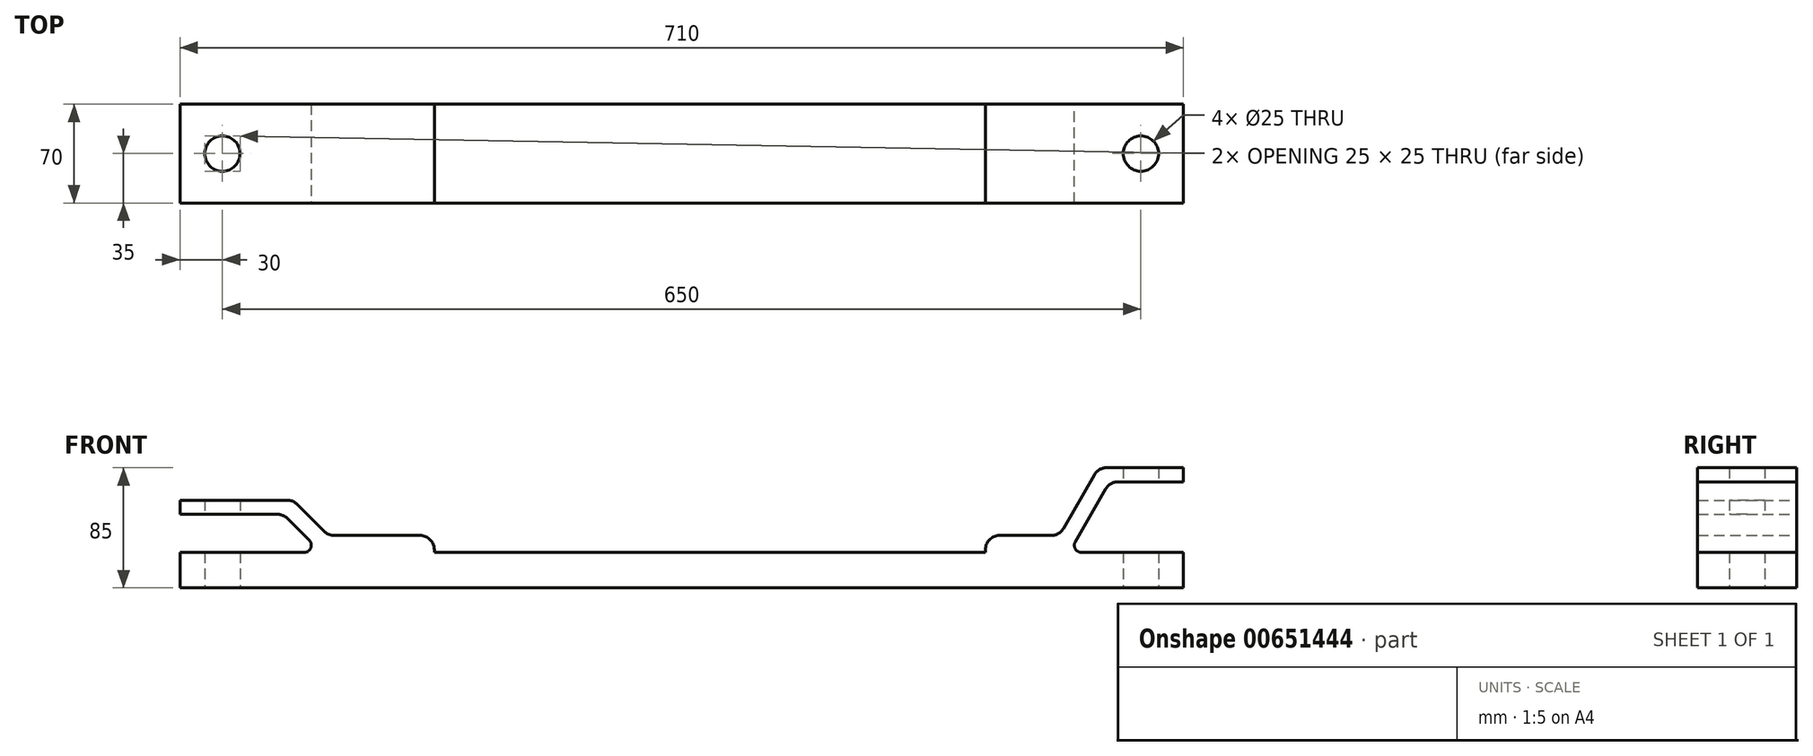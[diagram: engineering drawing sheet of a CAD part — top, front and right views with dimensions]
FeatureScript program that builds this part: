
annotation { "Feature Type Name" : "Feature", "Feature Type Description" : "" }
export const myFeature = defineFeature(function(context is Context, id is Id, definition is map)
    precondition{}
    {
        {
            var Q0;
            Q0=qCreatedBy(makeId("Front.planeOp"),FACE);
            var sketch = newSketch(context, id + "F0", { "sketchPlane" : qUnion([Q0])});
            skLineSegment(sketch, "E0.bottom", {"start": v(355, 0) * mm, "end": v(-355, 0) * mm});
            skLineSegment(sketch, "E0.top", {"start": v(355, 25) * mm, "end": v(-355, 25) * mm});
            skLineSegment(sketch, "E0.left", {"start": v(355, 0) * mm, "end": v(355, 25) * mm});
            skLineSegment(sketch, "E0.right", {"start": v(-355, 0) * mm, "end": v(-355, 25) * mm});
            skPoint(sketch, "E0.middle", {"position": v(0, 12.5) * mm});
            skLineSegment(sketch, "E1", {"start": v(-175, 25) * mm, "end": v(-175, 37) * mm});
            skLineSegment(sketch, "E2", {"start": v(-175, 37) * mm, "end": v(-250, 37) * mm});
            skLineSegment(sketch, "E3", {"start": v(-250, 37) * mm, "end": v(-275, 62) * mm});
            skLineSegment(sketch, "E4", {"start": v(-275, 62) * mm, "end": v(-355, 62) * mm});
            skLineSegment(sketch, "E5", {"start": v(-355, 62) * mm, "end": v(-355, 52) * mm});
            skLineSegment(sketch, "E6", {"start": v(-355, 52) * mm, "end": v(-281.97, 52) * mm});
            skLineSegment(sketch, "E7", {"start": v(-281.97, 52) * mm, "end": v(-254.97, 25) * mm});
            skLineSegment(sketch, "E8", {"start": v(215, 25) * mm, "end": v(215, 37) * mm});
            skLineSegment(sketch, "E9", {"start": v(215, 37) * mm, "end": v(267.29, 37) * mm});
            skLineSegment(sketch, "E10", {"start": v(267.29, 37) * mm, "end": v(295, 85) * mm});
            skLineSegment(sketch, "E11", {"start": v(295, 85) * mm, "end": v(355, 85) * mm});
            skLineSegment(sketch, "E12", {"start": v(355, 85) * mm, "end": v(355, 75) * mm});
            skLineSegment(sketch, "E13", {"start": v(355, 75) * mm, "end": v(303.08, 75) * mm});
            skLineSegment(sketch, "E14", {"start": v(303.08, 75) * mm, "end": v(274.22, 25) * mm});
            skSolve(sketch);
        }
        {
            var Q0;
            Q0 = qSketchRegion(id + "F0", true);
            extrude(context, id + "F1", {"entities" : qUnion([Q0]), "endBound" : BoundingType.SYMMETRIC, "depth" : 70 * mm, "offsetDistance" : 25 * mm});
        }
        {
            var Q0;
            Q0=makeQuery(id+"F1.opExtrude","SWEPT_EDGE",EDGE,{"disambiguationData":[OSD([sQuery(id+"F0.wireOp",EDGE,"E1"),sQuery(id+"F0.wireOp",EDGE,"E2")])]});
            var Q1;
            Q1=makeQuery(id+"F1.opExtrude","SWEPT_EDGE",EDGE,{"disambiguationData":[OSD([sQuery(id+"F0.wireOp",EDGE,"E2"),sQuery(id+"F0.wireOp",EDGE,"E3")])]});
            var Q2;
            Q2=makeQuery(id+"F1.opExtrude","SWEPT_EDGE",EDGE,{"disambiguationData":[OSD([sQuery(id+"F0.wireOp",EDGE,"E6"),sQuery(id+"F0.wireOp",EDGE,"E7")])]});
            var Q3;
            Q3=makeQuery(id+"F1.opExtrude","SWEPT_EDGE",EDGE,{"disambiguationData":[OSD([sQuery(id+"F0.wireOp",EDGE,"E3"),sQuery(id+"F0.wireOp",EDGE,"E4")])]});
            var Q4;
            Q4=makeQuery(id+"F1.opExtrude","SWEPT_EDGE",EDGE,{"disambiguationData":[OSD([sQuery(id+"F0.wireOp",EDGE,"E9"),sQuery(id+"F0.wireOp",EDGE,"E10")])]});
            var Q5;
            Q5=makeQuery(id+"F1.opExtrude","SWEPT_EDGE",EDGE,{"disambiguationData":[OSD([sQuery(id+"F0.wireOp",EDGE,"E10"),sQuery(id+"F0.wireOp",EDGE,"E11")])]});
            var Q6;
            Q6=makeQuery(id+"F1.opExtrude","SWEPT_EDGE",EDGE,{"disambiguationData":[OSD([sQuery(id+"F0.wireOp",EDGE,"E13"),sQuery(id+"F0.wireOp",EDGE,"E14")])]});
            var Q7;
            Q7=makeQuery(id+"F1.opExtrude","SWEPT_EDGE",EDGE,{"disambiguationData":[OSD([sQuery(id+"F0.wireOp",EDGE,"E8"),sQuery(id+"F0.wireOp",EDGE,"E9")])]});
            fillet(context, id + "F2", {"entities" : qUnion([Q0, Q1, Q2, Q3, Q4, Q5, Q6, Q7]), "radius" : 10 * mm, "tangentPropagation" : true, "allowEdgeOverflow" : false});
        }
        {
            var Q0;
            Q0=makeQuery(id+"F1.opExtrude","SWEPT_EDGE",EDGE,{"disambiguationData":[OSD([sQuery(id+"F0.wireOp",EDGE,"E0.top"),sQuery(id+"F0.wireOp",EDGE,"E7")])]});
            var Q1;
            Q1=makeQuery(id+"F1.opExtrude","SWEPT_EDGE",EDGE,{"disambiguationData":[OSD([sQuery(id+"F0.wireOp",EDGE,"E0.top"),sQuery(id+"F0.wireOp",EDGE,"E14")])]});
            fillet(context, id + "F3", {"entities" : qUnion([Q0, Q1]), "radius" : 5 * mm, "tangentPropagation" : true, "allowEdgeOverflow" : false});
        }
        {
            var Q0;
            Q0=qCreatedBy(makeId("Top.planeOp"),FACE);
            var sketch = newSketch(context, id + "F4", { "sketchPlane" : qUnion([Q0])});
            skCircle(sketch, "E15", {"center": v(-325, 0) * mm, "radius": 12.5 * mm});
            skCircle(sketch, "E16", {"center": v(325, 0) * mm, "radius": 12.5 * mm});
            skSolve(sketch);
        }
        {
            var Q0;
            Q0 = qSketchRegion(id + "F4", true);
            extrude(context, id + "F5", {"entities" : qUnion([Q0]), "operationType" : NewBodyOperationType.REMOVE, "endBound" : BoundingType.THROUGH_ALL, "depth" : 25 * mm, "offsetDistance" : 25 * mm});
        }
    });
